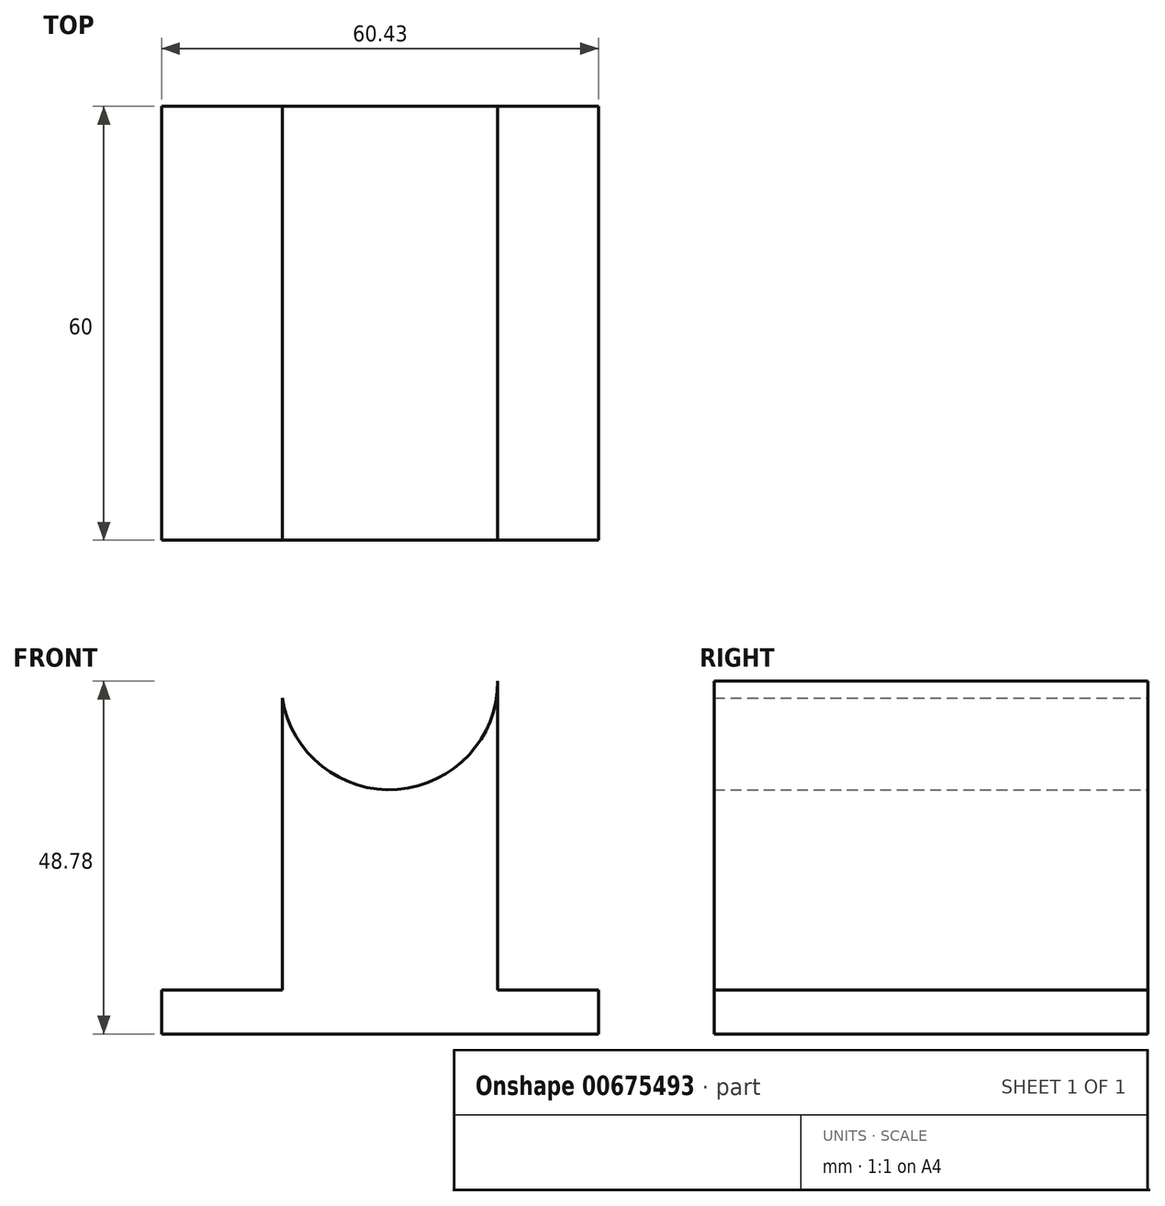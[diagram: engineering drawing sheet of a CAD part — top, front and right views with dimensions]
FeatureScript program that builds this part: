
annotation { "Feature Type Name" : "Feature", "Feature Type Description" : "" }
export const myFeature = defineFeature(function(context is Context, id is Id, definition is map)
    precondition{}
    {
        {
            var Q0;
            Q0=qCreatedBy(makeId("Front.planeOp"),FACE);
            var sketch = newSketch(context, id + "F0", { "sketchPlane" : qUnion([Q0])});
            skArc(sketch, "E0", {"start": v(-14.82, -2.3) * mm, "mid": v(1.16, -14.96) * mm, "end": v(15, 0) * mm});
            skLineSegment(sketch, "E1.left", {"start": v(15, 0) * mm, "end": v(15, -42.74) * mm});
            skLineSegment(sketch, "E1.right", {"start": v(-14.82, 0) * mm, "end": v(-14.82, -42.74) * mm});
            skLineSegment(sketch, "E2.bottom", {"start": v(-31.51, -42.74) * mm, "end": v(-14.82, -42.74) * mm});
            skLineSegment(sketch, "E2.top", {"start": v(-31.51, -48.78) * mm, "end": v(28.92, -48.78) * mm});
            skLineSegment(sketch, "E2.left", {"start": v(-31.51, -42.74) * mm, "end": v(-31.51, -48.78) * mm});
            skLineSegment(sketch, "E2.right", {"start": v(28.92, -42.74) * mm, "end": v(28.92, -48.78) * mm});
            skLineSegment(sketch, "E3.trimOffspring", {"start": v(15, -42.74) * mm, "end": v(28.92, -42.74) * mm});
            skSolve(sketch);
        }
        {
            var Q0;
            {var subQ2=sQuery(id+"F0.wireOp",EDGE,"E0");Q0=makeQuery(id+"F0.imprint","IMPRINT",FACE,{"disambiguationData":[TD([[makeQuery(id+"F0.imprint","IMPRINT",EDGE,{"derivedFrom":subQ2}),-1.0]])]});}
            extrude(context, id + "F1", {"entities" : qUnion([Q0]), "depth" : 60 * mm, "offsetDistance" : 25 * mm});
        }
    });
